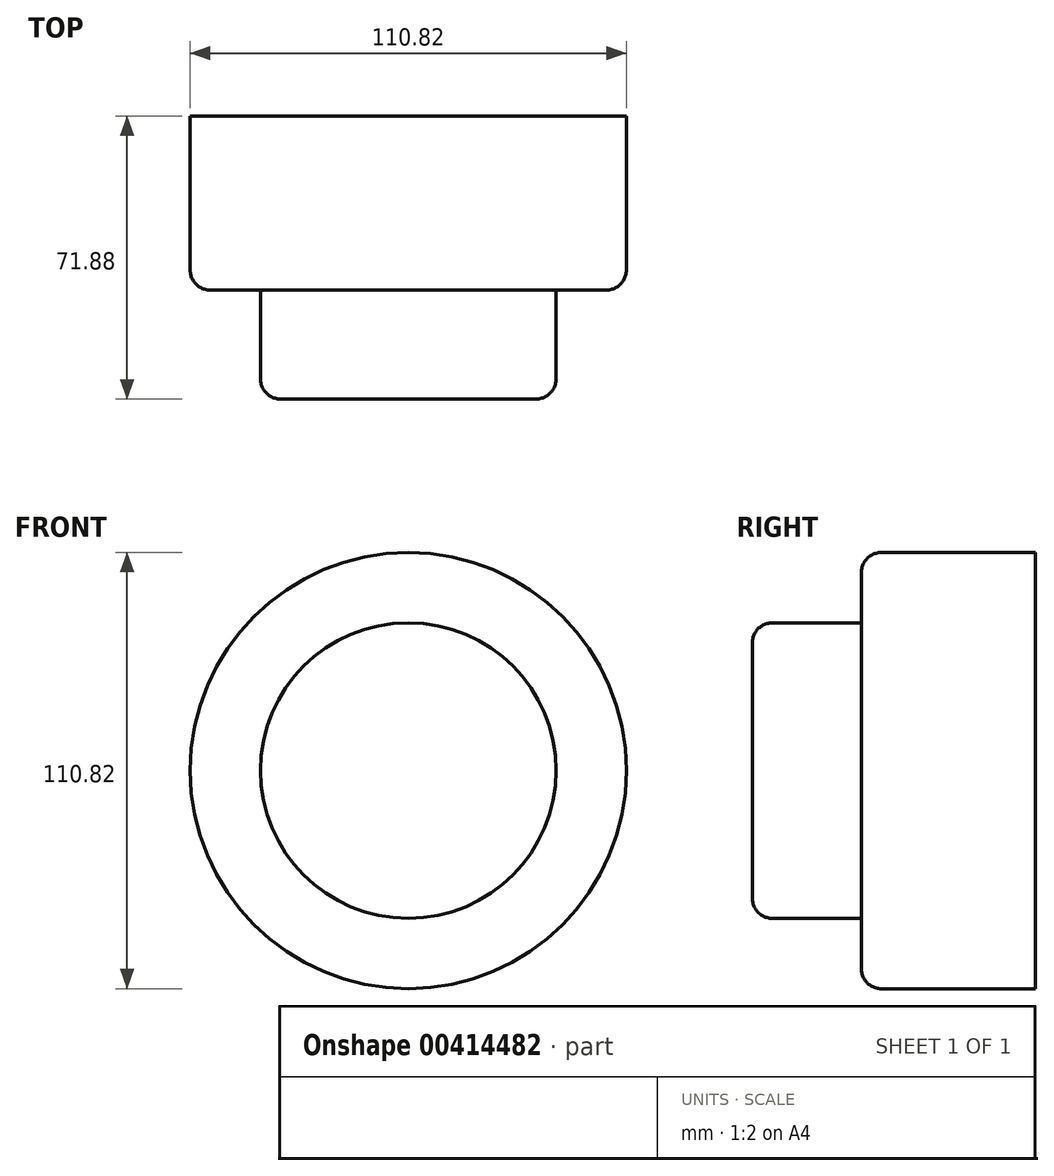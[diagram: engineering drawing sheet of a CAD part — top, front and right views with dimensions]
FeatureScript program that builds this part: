
annotation { "Feature Type Name" : "Feature", "Feature Type Description" : "" }
export const myFeature = defineFeature(function(context is Context, id is Id, definition is map)
    precondition{}
    {
        {
            var Q0;
            Q0=qCreatedBy(makeId("Front.planeOp"),FACE);
            var sketch = newSketch(context, id + "F0", { "sketchPlane" : qUnion([Q0])});
            skCircle(sketch, "E0", {"center": v(0, 0) * mm, "radius": 55.4 * mm});
            skSolve(sketch);
        }
        {
            var Q0;
            Q0=makeQuery(id+"F0.imprint","IMPRINT",FACE,{"disambiguationData":[TD([[makeQuery(id+"F0.imprint","IMPRINT",EDGE,{"derivedFrom":sQuery(id+"F0.wireOp",EDGE,"E0")}),1.0]])]});
            extrude(context, id + "F1", {"entities" : qUnion([Q0]), "depth" : 44.2 * mm});
        }
        {
            var Q0;
            Q0=qCreatedBy(makeId("Front.planeOp"),FACE);
            var sketch = newSketch(context, id + "F2", { "sketchPlane" : qUnion([Q0])});
            skCircle(sketch, "E1", {"center": v(0, 0) * mm, "radius": 37.54 * mm});
            skSolve(sketch);
        }
        {
            var Q0;
            Q0 = qSketchRegion(id + "F2", true);
            extrude(context, id + "F3", {"entities" : qUnion([Q0]), "operationType" : NewBodyOperationType.ADD, "depth" : 71.88 * mm});
        }
        {
            var Q0;
            Q0=makeQuery(id+"F3.opExtrude","CAP_EDGE",EDGE,{"disambiguationData":[OSD([sQuery(id+"F2.wireOp",EDGE,"E1")])],"isStart":false});
            var Q1;
            Q1=makeQuery(id+"F1.opExtrude","CAP_EDGE",EDGE,{"disambiguationData":[OSD([sQuery(id+"F0.wireOp",EDGE,"E0")])],"isStart":false});
            fillet(context, id + "F4", {"entities" : qUnion([Q0, Q1]), "radius" : 5.08 * mm, "tangentPropagation" : true, "allowEdgeOverflow" : false});
        }
    });
